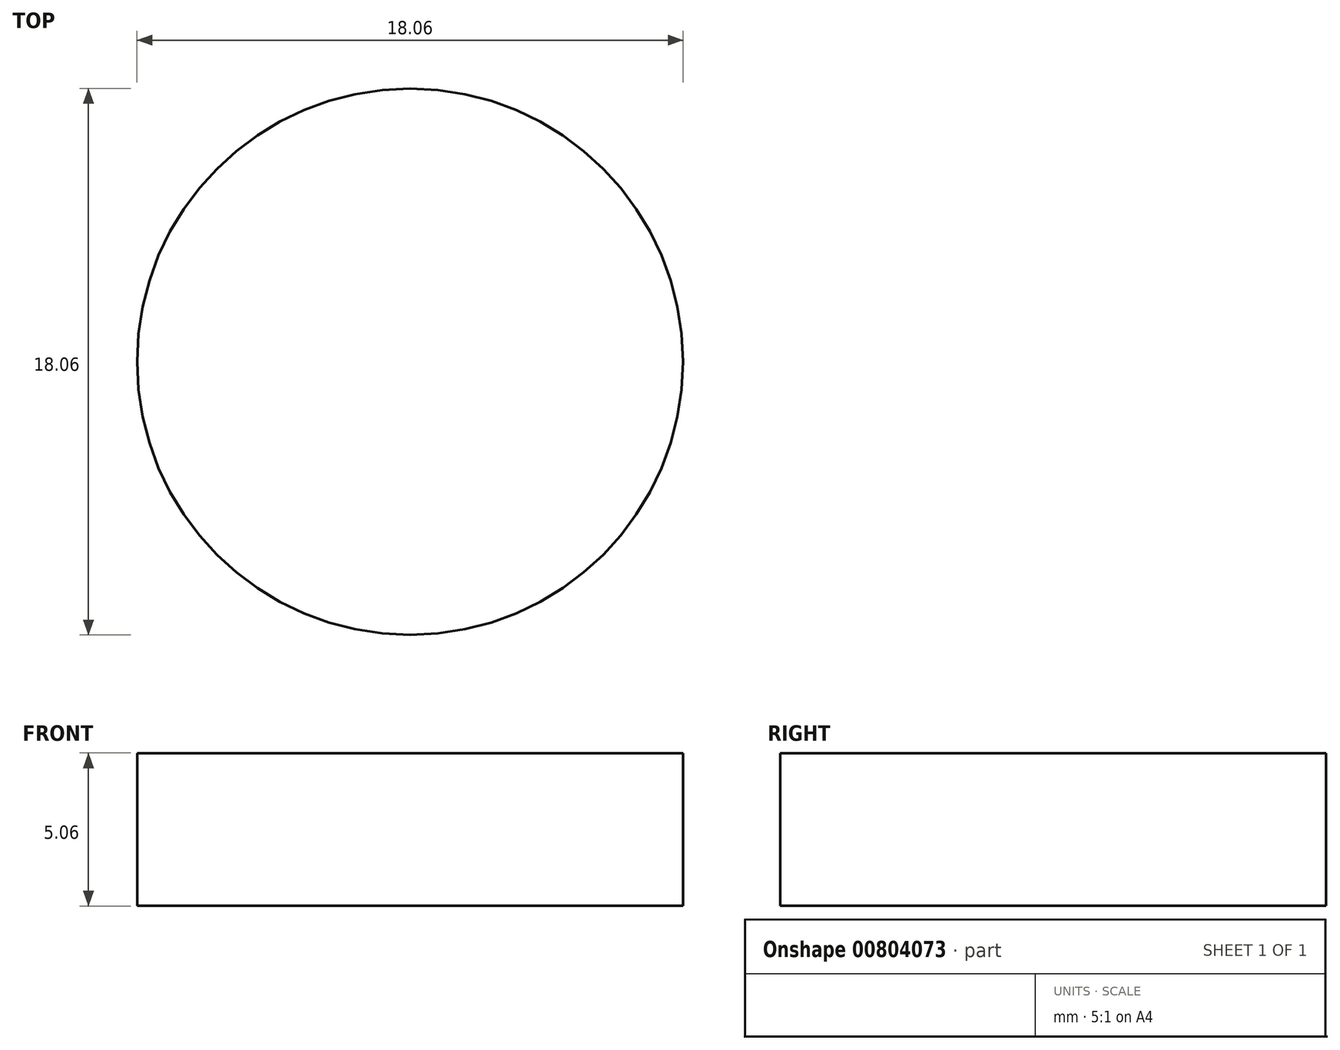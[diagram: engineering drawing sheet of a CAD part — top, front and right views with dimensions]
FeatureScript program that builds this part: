
annotation { "Feature Type Name" : "Feature", "Feature Type Description" : "" }
export const myFeature = defineFeature(function(context is Context, id is Id, definition is map)
    precondition{}
    {
        {
            var Q0;
            Q0=qCreatedBy(makeId("Top.planeOp"),FACE);
            var sketch = newSketch(context, id + "F0", { "sketchPlane" : qUnion([Q0])});
            skCircle(sketch, "E0", {"center": v(0, 0) * mm, "radius": 9.02 * mm});
            skSolve(sketch);
        }
        {
            var Q0;
            Q0 = qSketchRegion(id + "F0", true);
            extrude(context, id + "F1", {"entities" : qUnion([Q0]), "endBound" : BoundingType.SYMMETRIC, "depth" : 5.05 * mm, "offsetDistance" : 25 * mm});
        }
    });
